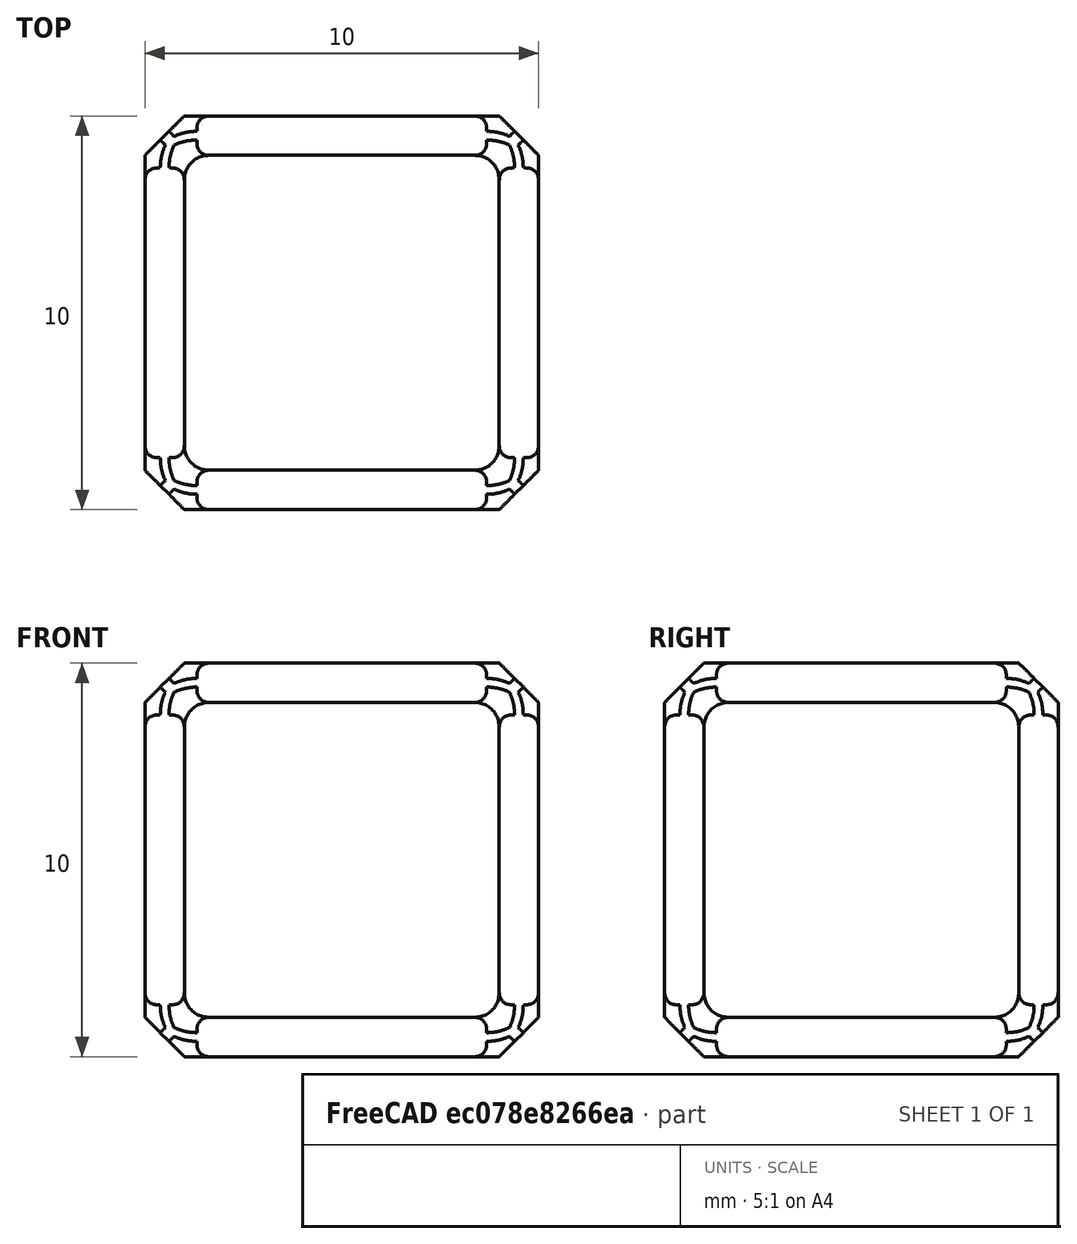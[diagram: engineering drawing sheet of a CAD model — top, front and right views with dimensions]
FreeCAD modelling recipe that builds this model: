
FCSTD DOCUMENT  (FreeCAD 0.18.4R)
Label: 10x10x10xTestCube
License: All rights reserved
LicenseURL: http://en.wikipedia.org/wiki/All_rights_reserved
objects: PartDesign::AdditiveBox×1, PartDesign::Chamfer×1, PartDesign::Fillet×1, PartDesign::Body×1, App::Part×1
note: 5 computed .brp shape members not serialized (recipe doc carries the construction recipe); baked Part::Feature solids carry a one-line shape summary decoded from their .brp

FEATURE [PartDesign::AdditiveBox] Box
  AttacherType = Attacher::AttachEngine3D
  Height = 10
  Length = 10
  Width = 10
FEATURE [PartDesign::Chamfer] Chamfer
  Base = -> Box [Face1,Face3,Edge9,Face5,Face2,Face4,Face6]
  BaseFeature = -> Box
  Size = 1
FEATURE [PartDesign::Fillet] Fillet
  Base = -> Chamfer [Face6,Face22,Face25,Face24,Face8,Face12,Face26,Face10]
  BaseFeature = -> Chamfer
  Radius = 1
FEATURE [PartDesign::Body] Body
  Group = -> [Box,Chamfer,Fillet]
  Origin = -> Origin001
  Tip = -> Fillet
FEATURE [App::Part] Part
  Group = -> [Body]
  Origin = -> Origin
